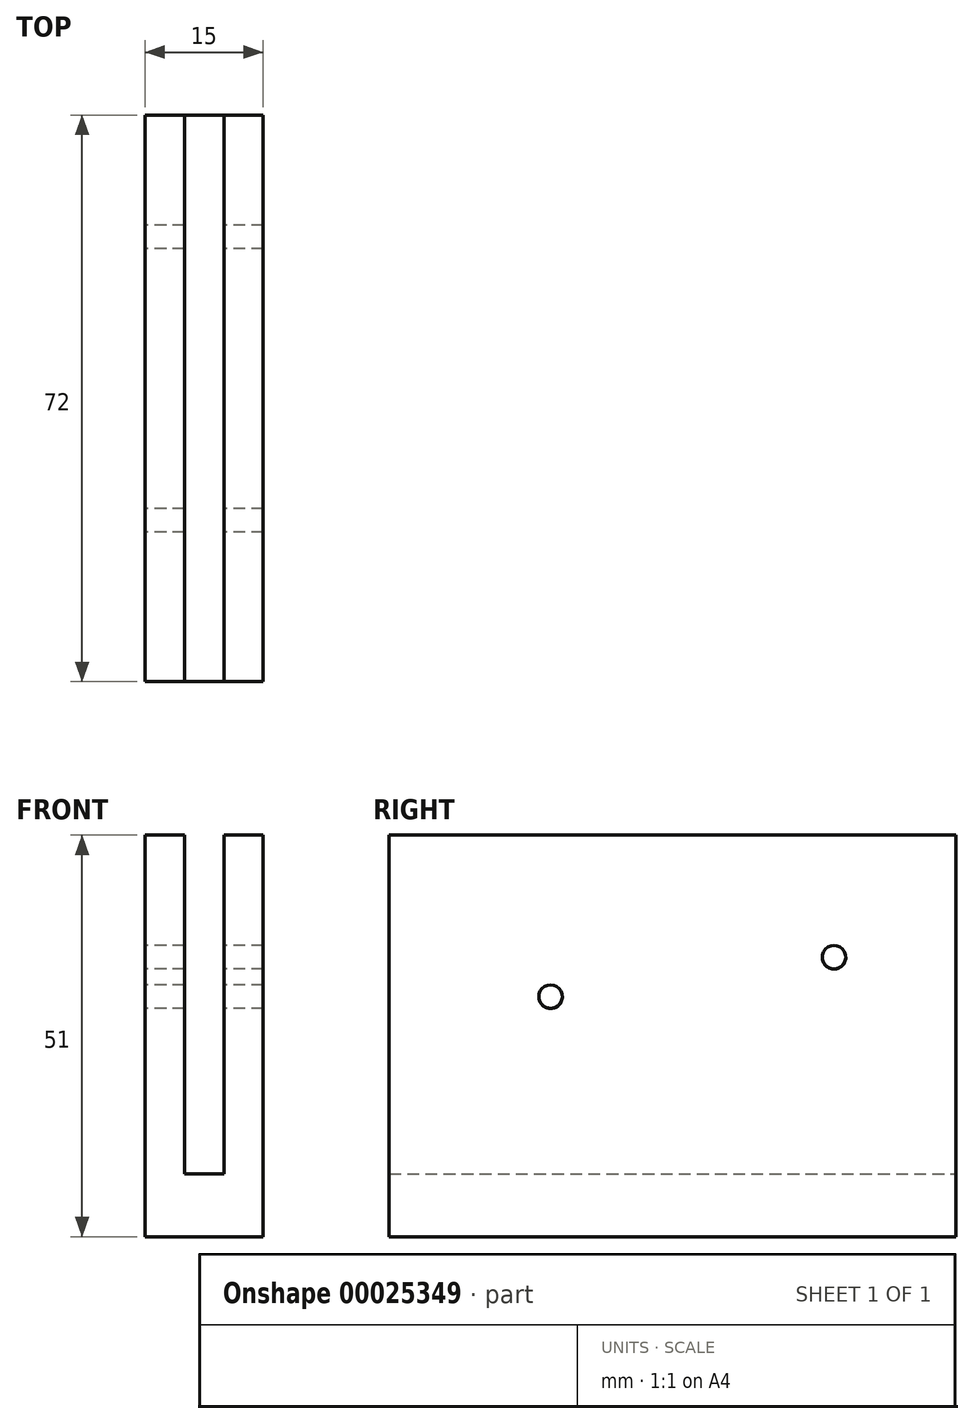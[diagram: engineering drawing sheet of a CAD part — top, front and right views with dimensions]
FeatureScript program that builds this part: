
annotation { "Feature Type Name" : "Feature", "Feature Type Description" : "" }
export const myFeature = defineFeature(function(context is Context, id is Id, definition is map)
    precondition{}
    {
        {
            var Q0;
            Q0=qCreatedBy(makeId("Front.planeOp"),FACE);
            var sketch = newSketch(context, id + "F0", { "sketchPlane" : qUnion([Q0])});
            skLineSegment(sketch, "E0.rect.bottom", {"start": v(2.5, -21.5) * mm, "end": v(-2.5, -21.5) * mm});
            skLineSegment(sketch, "E0.rect.left", {"start": v(2.5, -21.5) * mm, "end": v(2.5, 21.5) * mm});
            skLineSegment(sketch, "E0.rect.right", {"start": v(-2.5, -21.5) * mm, "end": v(-2.5, 21.5) * mm});
            skPoint(sketch, "E0.rect.middle", {"position": v(0, 0) * mm});
            skLineSegment(sketch, "E1.rect.bottom", {"start": v(7.5, -29.5) * mm, "end": v(-7.5, -29.5) * mm});
            skLineSegment(sketch, "E1.rect.left", {"start": v(7.5, -29.5) * mm, "end": v(7.5, 21.5) * mm});
            skLineSegment(sketch, "E1.rect.right", {"start": v(-7.5, -29.5) * mm, "end": v(-7.5, 21.5) * mm});
            skLineSegment(sketch, "E2", {"start": v(-2.5, 21.5) * mm, "end": v(-7.5, 21.5) * mm});
            skLineSegment(sketch, "E3", {"start": v(-7.5, 21.5) * mm, "end": v(-2.5, 21.5) * mm});
            skPoint(sketch, "E4.orphan", {"position": v(-7.5, 29.5) * mm});
            skPoint(sketch, "E5.orphan", {"position": v(7.5, 29.5) * mm});
            skLineSegment(sketch, "E6.trimOffspring", {"start": v(2.5, 21.5) * mm, "end": v(7.5, 21.5) * mm});
            skSolve(sketch);
        }
        {
            var Q0;
            Q0 = qSketchRegion(id + "F0", true);
            extrude(context, id + "F1", {"entities" : qUnion([Q0]), "endBound" : BoundingType.SYMMETRIC, "depth" : 72 * mm});
        }
        {
            var Q0;
            Q0=makeQuery(id+"F1.opExtrude","SWEPT_FACE",FACE,{"disambiguationData":[OSD([sQuery(id+"F0.wireOp",EDGE,"E1.rect.right")])]});
            var sketch = newSketch(context, id + "F2", { "sketchPlane" : qUnion([Q0])});
            skPoint(sketch, "E7", {"position": v(-20.5, 21.5) * mm});
            skPoint(sketch, "E8", {"position": v(15.5, 21.5) * mm});
            skPoint(sketch, "E9", {"position": v(-36, 6) * mm});
            skPoint(sketch, "E10", {"position": v(-36, 1) * mm});
            skCircle(sketch, "E11", {"center": v(-20.5, 6) * mm, "radius": 1.5 * mm});
            skCircle(sketch, "E12", {"center": v(15.5, 1) * mm, "radius": 1.5 * mm});
            skSolve(sketch);
        }
        {
            var Q0;
            Q0 = qSketchRegion(id + "F2", true);
            extrude(context, id + "F3", {"entities" : qUnion([Q0]), "operationType" : NewBodyOperationType.REMOVE, "oppositeDirection" : true, "depth" : 25 * mm});
        }
    });
